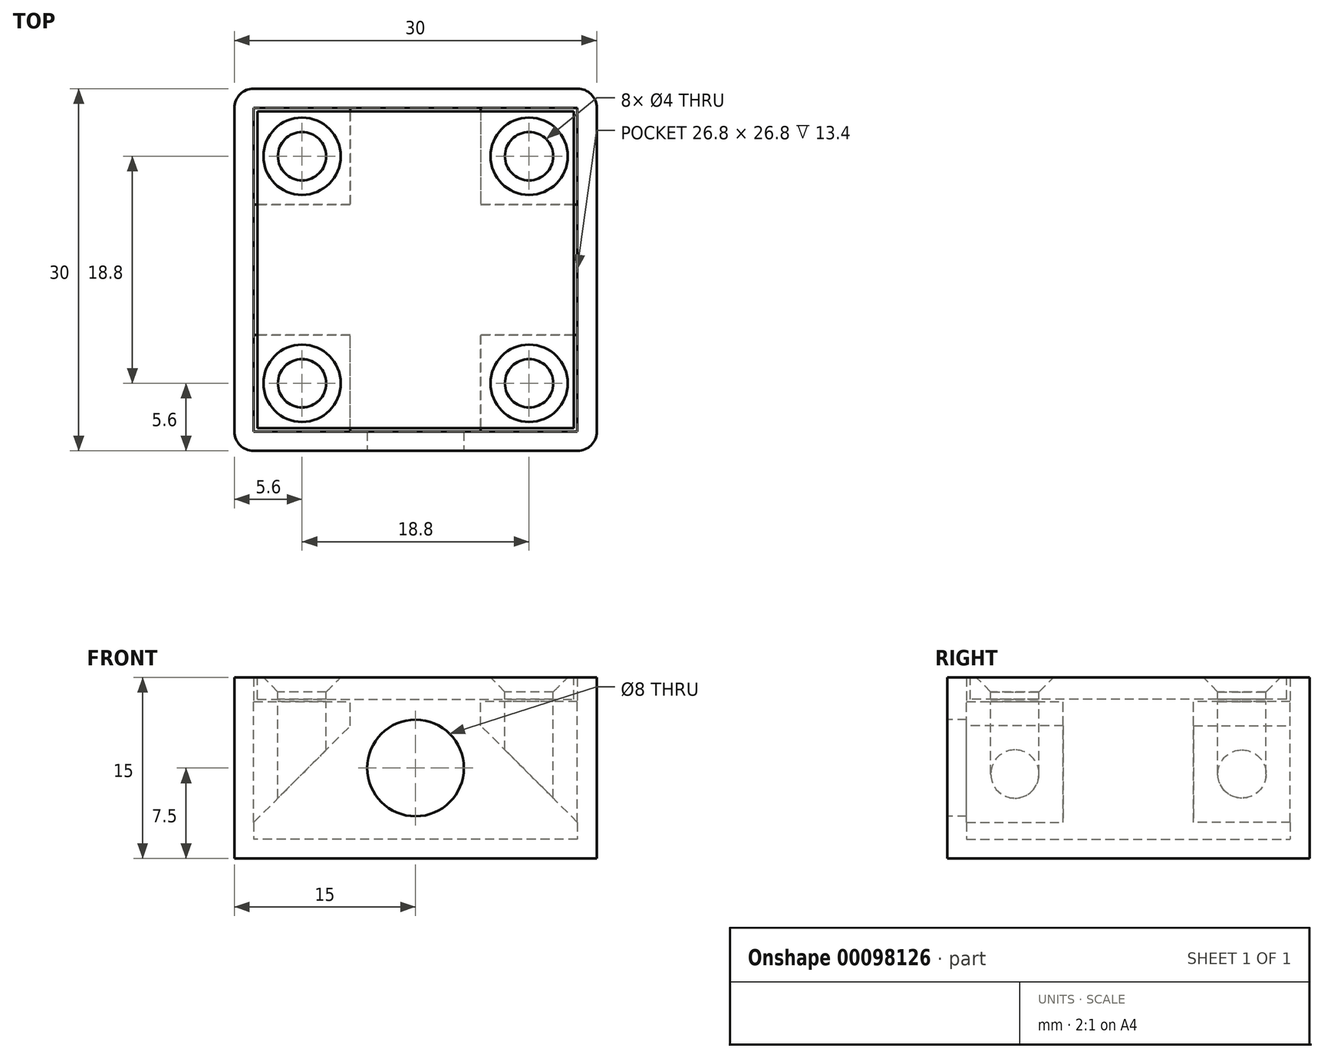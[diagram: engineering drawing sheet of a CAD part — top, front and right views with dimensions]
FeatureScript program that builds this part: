
annotation { "Feature Type Name" : "Feature", "Feature Type Description" : "" }
export const myFeature = defineFeature(function(context is Context, id is Id, definition is map)
    precondition{}
    {
        {
            var Q0;
            Q0=qCreatedBy(makeId("Top.planeOp"),FACE);
            var sketch = newSketch(context, id + "F0", { "sketchPlane" : qUnion([Q0])});
            skLineSegment(sketch, "E0.bottom", {"start": v(0, 0) * mm, "end": v(-30, 0) * mm});
            skLineSegment(sketch, "E0.top", {"start": v(0, 30) * mm, "end": v(-30, 30) * mm});
            skLineSegment(sketch, "E0.left", {"start": v(0, 0) * mm, "end": v(0, 30) * mm});
            skLineSegment(sketch, "E0.right", {"start": v(-30, 0) * mm, "end": v(-30, 30) * mm});
            skSolve(sketch);
        }
        {
            var Q0;
            Q0=makeQuery(id+"F0.imprint","IMPRINT",FACE,{"disambiguationData":[TD([[makeQuery(id+"F0.imprint","IMPRINT",EDGE,{"derivedFrom":sQuery(id+"F0.wireOp",EDGE,"E0.bottom")}),-1.0]])]});
            extrude(context, id + "F1", {"entities" : qUnion([Q0]), "depth" : 15 * mm});
        }
        {
            var Q0;
            Q0=makeQuery(id+"F1.opExtrude","CAP_FACE",FACE,{"disambiguationData":[OSD([sQuery(id+"F0.wireOp",EDGE,"E0.bottom"),sQuery(id+"F0.wireOp",EDGE,"E0.top"),sQuery(id+"F0.wireOp",EDGE,"E0.left"),sQuery(id+"F0.wireOp",EDGE,"E0.right")])],"isStart":false});
            shell(context, id + "F2", {"entities" : qUnion([Q0]), "thickness" : 1.6 * mm});
        }
        {
            var Q0;
            Q0=makeQuery(id+"F1.opExtrude","CAP_FACE",FACE,{"disambiguationData":[OSD([sQuery(id+"F0.wireOp",EDGE,"E0.bottom"),sQuery(id+"F0.wireOp",EDGE,"E0.top"),sQuery(id+"F0.wireOp",EDGE,"E0.left"),sQuery(id+"F0.wireOp",EDGE,"E0.right")])],"isStart":false});
            cPlane(context, id + "F3", {"entities" : qUnion([Q0]), "cplaneType" : CPlaneType.OFFSET, "offset" : 2 * mm, "oppositeDirection" : true, "width" : 150 * mm, "height" : 150 * mm});
        }
        {
            var Q0;
            Q0=qCreatedBy(id+"F3.planeOp",FACE);
            var sketch = newSketch(context, id + "F4", { "sketchPlane" : qUnion([Q0])});
            skLineSegment(sketch, "E1.bottom", {"start": v(-28.4, 28.4) * mm, "end": v(-20.4, 28.4) * mm});
            skLineSegment(sketch, "E1.top", {"start": v(-28.4, 20.4) * mm, "end": v(-20.4, 20.4) * mm});
            skLineSegment(sketch, "E1.left", {"start": v(-28.4, 28.4) * mm, "end": v(-28.4, 20.4) * mm});
            skLineSegment(sketch, "E1.right", {"start": v(-20.4, 28.4) * mm, "end": v(-20.4, 20.4) * mm});
            skLineSegment(sketch, "E2.bottom", {"start": v(-1.6, 28.4) * mm, "end": v(-9.6, 28.4) * mm});
            skLineSegment(sketch, "E2.top", {"start": v(-1.6, 20.4) * mm, "end": v(-9.6, 20.4) * mm});
            skLineSegment(sketch, "E2.left", {"start": v(-1.6, 28.4) * mm, "end": v(-1.6, 20.4) * mm});
            skLineSegment(sketch, "E2.right", {"start": v(-9.6, 28.4) * mm, "end": v(-9.6, 20.4) * mm});
            skLineSegment(sketch, "E3.bottom", {"start": v(-1.6, 1.6) * mm, "end": v(-9.6, 1.6) * mm});
            skLineSegment(sketch, "E3.top", {"start": v(-1.6, 9.6) * mm, "end": v(-9.6, 9.6) * mm});
            skLineSegment(sketch, "E3.left", {"start": v(-1.6, 1.6) * mm, "end": v(-1.6, 9.6) * mm});
            skLineSegment(sketch, "E3.right", {"start": v(-9.6, 1.6) * mm, "end": v(-9.6, 9.6) * mm});
            skLineSegment(sketch, "E4.bottom", {"start": v(-28.4, 1.6) * mm, "end": v(-20.4, 1.6) * mm});
            skLineSegment(sketch, "E4.top", {"start": v(-28.4, 9.6) * mm, "end": v(-20.4, 9.6) * mm});
            skLineSegment(sketch, "E4.left", {"start": v(-28.4, 1.6) * mm, "end": v(-28.4, 9.6) * mm});
            skLineSegment(sketch, "E4.right", {"start": v(-20.4, 1.6) * mm, "end": v(-20.4, 9.6) * mm});
            skCircle(sketch, "E5", {"center": v(-24.4, 24.4) * mm, "radius": 2 * mm});
            skPoint(sketch, "E5.centerSnap0", {"position": v(-20.4, 24.4) * mm});
            skPoint(sketch, "E5.centerSnap1", {"position": v(-24.4, 28.4) * mm});
            skCircle(sketch, "E6", {"center": v(-5.6, 24.4) * mm, "radius": 2 * mm});
            skPoint(sketch, "E6.centerSnap0", {"position": v(-5.6, 20.4) * mm});
            skPoint(sketch, "E6.centerSnap1", {"position": v(-9.6, 24.4) * mm});
            skCircle(sketch, "E7", {"center": v(-5.6, 5.6) * mm, "radius": 2 * mm});
            skPoint(sketch, "E7.centerSnap0", {"position": v(-9.6, 5.6) * mm});
            skPoint(sketch, "E7.centerSnap1", {"position": v(-5.6, 9.6) * mm});
            skCircle(sketch, "E8", {"center": v(-24.4, 5.6) * mm, "radius": 2 * mm});
            skPoint(sketch, "E9", {"position": v(-24.4, 9.6) * mm});
            skPoint(sketch, "E10", {"position": v(-20.4, 5.6) * mm});
            skSolve(sketch);
        }
        {
            var Q0;
            Q0 = qSketchRegion(id + "F4", true);
            extrude(context, id + "F5", {"entities" : qUnion([Q0]), "operationType" : NewBodyOperationType.ADD, "oppositeDirection" : true, "depth" : 10 * mm});
        }
        {
            var Q0;
            Q0=makeQuery(id+"F5.opExtrude","CAP_EDGE",EDGE,{"disambiguationData":[OSD([sQuery(id+"F4.wireOp",EDGE,"E1.right")])],"isStart":false});
            var Q1;
            Q1=makeQuery(id+"F5.opExtrude","CAP_EDGE",EDGE,{"disambiguationData":[OSD([sQuery(id+"F4.wireOp",EDGE,"E2.right")])],"isStart":false});
            var Q2;
            Q2=makeQuery(id+"F5.opExtrude","CAP_EDGE",EDGE,{"disambiguationData":[OSD([sQuery(id+"F4.wireOp",EDGE,"E3.right")])],"isStart":false});
            var Q3;
            Q3=makeQuery(id+"F5.opExtrude","CAP_EDGE",EDGE,{"disambiguationData":[OSD([sQuery(id+"F4.wireOp",EDGE,"E4.right")])],"isStart":false});
            chamfer(context, id + "F6", {"entities" : qUnion([Q0, Q1, Q2, Q3]), "width" : 8 * mm, "tangentPropagation" : true});
        }
        {
            var Q0;
            Q0=makeQuery(id+"F1.opExtrude","SWEPT_FACE",FACE,{"disambiguationData":[OSD([sQuery(id+"F0.wireOp",EDGE,"E0.bottom")])]});
            var sketch = newSketch(context, id + "F7", { "sketchPlane" : qUnion([Q0])});
            skCircle(sketch, "E11", {"center": v(-15, 7.5) * mm, "radius": 4 * mm});
            skPoint(sketch, "E12", {"position": v(-15, 0) * mm});
            skPoint(sketch, "E13", {"position": v(-30, 7.5) * mm});
            skSolve(sketch);
        }
        {
            var Q0;
            Q0 = qSketchRegion(id + "F7", true);
            var Q1;
            Q1=makeQuery(id+"F2.opShell","OFFSET_FACE",FACE,{"disambiguationData":[OSD([sQuery(id+"F0.wireOp",EDGE,"E0.bottom")])]});
            extrude(context, id + "F8", {"entities" : qUnion([Q0]), "operationType" : NewBodyOperationType.REMOVE, "endBound" : BoundingType.UP_TO_SURFACE, "oppositeDirection" : true, "endBoundEntityFace" : qUnion([Q1]), "depth" : 25 * mm});
        }
        {
            var Q0;
            Q0=makeQuery(id+"F1.opExtrude","CAP_FACE",FACE,{"disambiguationData":[OSD([sQuery(id+"F0.wireOp",EDGE,"E0.bottom"),sQuery(id+"F0.wireOp",EDGE,"E0.top"),sQuery(id+"F0.wireOp",EDGE,"E0.left"),sQuery(id+"F0.wireOp",EDGE,"E0.right")])],"isStart":false});
            var sketch = newSketch(context, id + "F9", { "sketchPlane" : qUnion([Q0])});
            skLineSegment(sketch, "E14.bottom", {"start": v(-28.1, 28.1) * mm, "end": v(-1.9, 28.1) * mm});
            skLineSegment(sketch, "E14.top", {"start": v(-28.1, 1.9) * mm, "end": v(-1.9, 1.9) * mm});
            skLineSegment(sketch, "E14.left", {"start": v(-28.1, 28.1) * mm, "end": v(-28.1, 1.9) * mm});
            skLineSegment(sketch, "E14.right", {"start": v(-1.9, 28.1) * mm, "end": v(-1.9, 1.9) * mm});
            skCircle(sketch, "E15", {"center": v(-24.4, 24.4) * mm, "radius": 2 * mm});
            skCircle(sketch, "E16", {"center": v(-5.6, 24.4) * mm, "radius": 2 * mm});
            skCircle(sketch, "E17", {"center": v(-5.6, 5.6) * mm, "radius": 2 * mm});
            skCircle(sketch, "E18", {"center": v(-24.4, 5.6) * mm, "radius": 2 * mm});
            skSolve(sketch);
        }
        {
            var Q0;
            Q0 = qSketchRegion(id + "F9", true);
            extrude(context, id + "F10", {"entities" : qUnion([Q0]), "oppositeDirection" : true, "depth" : 1.8 * mm});
        }
        {
            var Q0;
            Q0=makeQuery(id+"F10.opExtrude","CAP_EDGE",EDGE,{"disambiguationData":[OSD([sQuery(id+"F9.wireOp",EDGE,"E16")])],"isStart":true});
            var Q1;
            Q1=makeQuery(id+"F10.opExtrude","CAP_EDGE",EDGE,{"disambiguationData":[OSD([sQuery(id+"F9.wireOp",EDGE,"E17")])],"isStart":true});
            var Q2;
            Q2=makeQuery(id+"F10.opExtrude","CAP_EDGE",EDGE,{"disambiguationData":[OSD([sQuery(id+"F9.wireOp",EDGE,"E18")])],"isStart":true});
            var Q3;
            Q3=makeQuery(id+"F10.opExtrude","CAP_EDGE",EDGE,{"disambiguationData":[OSD([sQuery(id+"F9.wireOp",EDGE,"E15")])],"isStart":true});
            chamfer(context, id + "F11", {"entities" : qUnion([Q0, Q1, Q2, Q3]), "width" : 1.2 * mm, "tangentPropagation" : true});
        }
        {
            var Q0;
            Q0=makeQuery(id+"F1.opExtrude","SWEPT_EDGE",EDGE,{"disambiguationData":[OSD([sQuery(id+"F0.wireOp",EDGE,"E0.top"),sQuery(id+"F0.wireOp",EDGE,"E0.left")])]});
            var Q1;
            Q1=makeQuery(id+"F1.opExtrude","SWEPT_EDGE",EDGE,{"disambiguationData":[OSD([sQuery(id+"F0.wireOp",EDGE,"E0.top"),sQuery(id+"F0.wireOp",EDGE,"E0.right")])]});
            var Q2;
            Q2=makeQuery(id+"F1.opExtrude","SWEPT_EDGE",EDGE,{"disambiguationData":[OSD([sQuery(id+"F0.wireOp",EDGE,"E0.bottom"),sQuery(id+"F0.wireOp",EDGE,"E0.right")])]});
            var Q3;
            Q3=makeQuery(id+"F1.opExtrude","SWEPT_EDGE",EDGE,{"disambiguationData":[OSD([sQuery(id+"F0.wireOp",EDGE,"E0.bottom"),sQuery(id+"F0.wireOp",EDGE,"E0.left")])]});
            fillet(context, id + "F12", {"entities" : qUnion([Q0, Q1, Q2, Q3]), "radius" : 1.6 * mm, "tangentPropagation" : true, "allowEdgeOverflow" : false});
        }
    });
